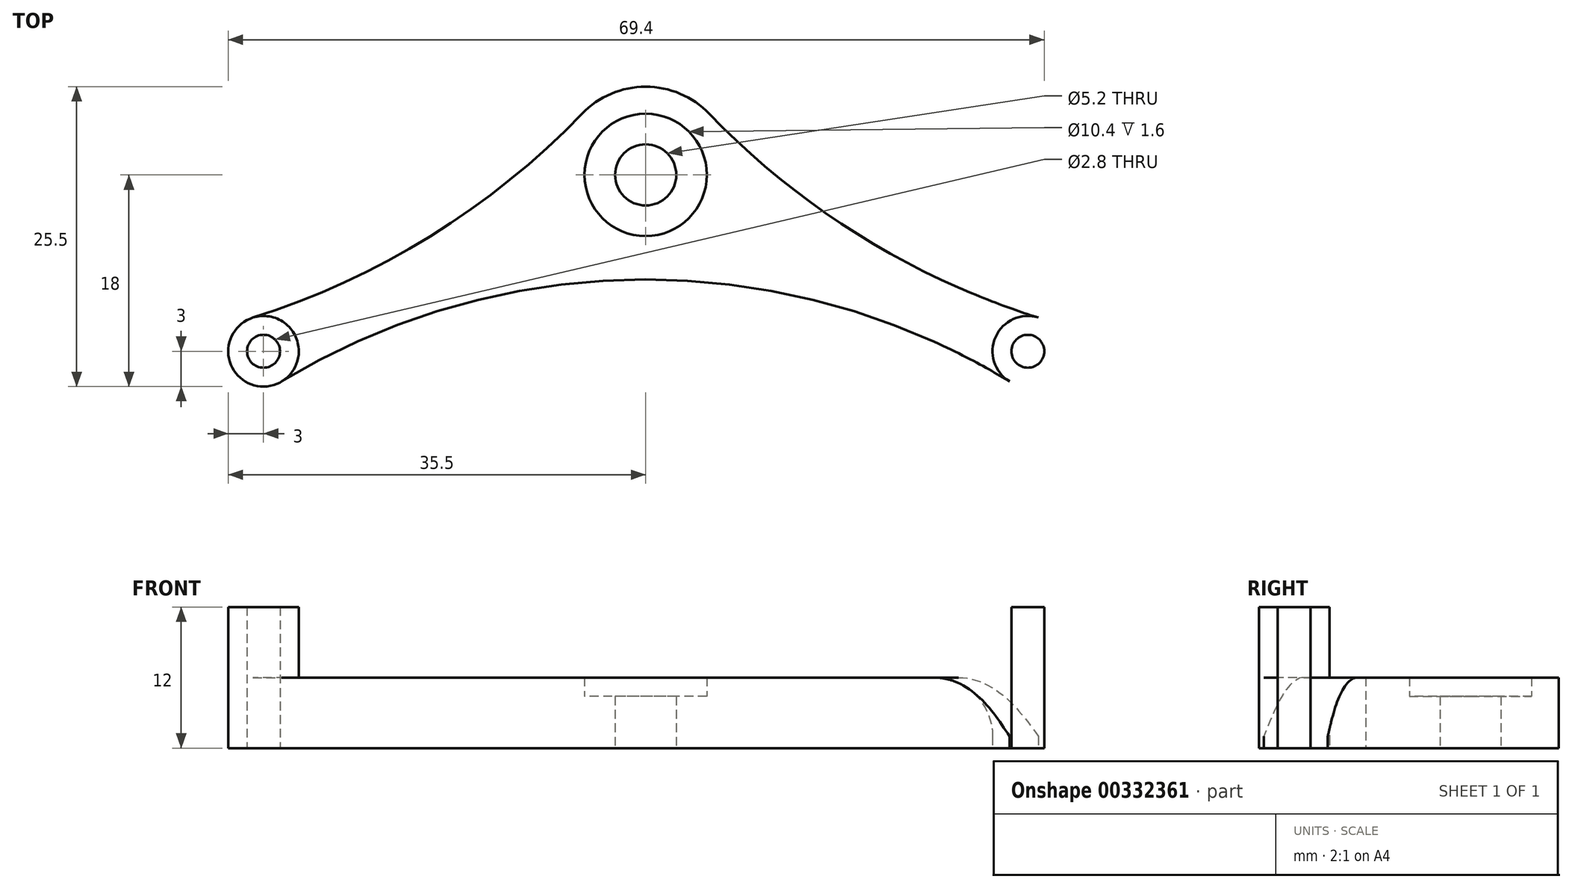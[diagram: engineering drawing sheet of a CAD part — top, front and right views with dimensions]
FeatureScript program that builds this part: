
annotation { "Feature Type Name" : "Feature", "Feature Type Description" : "" }
export const myFeature = defineFeature(function(context is Context, id is Id, definition is map)
    precondition{}
    {
        {
            var Q0;
            Q0=qCreatedBy(makeId("Top.planeOp"),FACE);
            var sketch = newSketch(context, id + "F0", { "sketchPlane" : qUnion([Q0])});
            skCircle(sketch, "E0", {"center": v(-32.5, 0) * mm, "radius": 1.4 * mm});
            skCircle(sketch, "E1.MirrorC", {"center": v(32.5, 0) * mm, "radius": 1.4 * mm});
            skCircle(sketch, "E2", {"center": v(-32.5, 0) * mm, "radius": 3 * mm});
            skCircle(sketch, "E3", {"center": v(0, 15) * mm, "radius": 2.6 * mm});
            skCircle(sketch, "E4", {"center": v(0, 15) * mm, "radius": 5.2 * mm});
            skCircle(sketch, "E5", {"center": v(0, 15) * mm, "radius": 7.5 * mm});
            skArc(sketch, "E6", {"start": v(-33.4, 2.86) * mm, "mid": v(-18.31, 9.78) * mm, "end": v(-5.4, 20.2) * mm});
            skArc(sketch, "E7.MirrorCS", {"start": v(33.4, 2.86) * mm, "mid": v(18.31, 9.78) * mm, "end": v(5.4, 20.2) * mm});
            skCircle(sketch, "E8.MirrorC", {"center": v(32.5, 0) * mm, "radius": 3 * mm});
            skArc(sketch, "E9", {"start": v(30.94, -2.56) * mm, "mid": v(0, 6.1) * mm, "end": v(-30.94, -2.56) * mm});
            skSolve(sketch);
        }
        {
            var Q0;
            Q0=makeQuery(id+"F0.imprint","IMPRINT",FACE,{"disambiguationData":[TD([[makeQuery(id+"F0.imprint","IMPRINT",EDGE,{"derivedFrom":sQuery(id+"F0.wireOp",EDGE,"E3")}),-1.0]])]});
            extrude(context, id + "F1", {"entities" : qUnion([Q0]), "depth" : 4.4 * mm, "offsetDistance" : 25 * mm});
        }
        {
            var Q0;
            {var subQ0=sQuery(id+"F0.wireOp",EDGE,"E6");Q0=makeQuery(id+"F0.imprint","IMPRINT",FACE,{"disambiguationData":[TD([[makeQuery(id+"F0.imprint","IMPRINT",EDGE,{"derivedFrom":subQ0}),-1.0]])]});}
            var Q1;
            Q1=makeQuery(id+"F0.imprint","IMPRINT",FACE,{"disambiguationData":[TD([[makeQuery(id+"F0.imprint","IMPRINT",EDGE,{"derivedFrom":sQuery(id+"F0.wireOp",EDGE,"E4")}),-1.0]])]});
            var Q2;
            {var subQ1=sQuery(id+"F0.wireOp",EDGE,"E7.MirrorCS");Q2=makeQuery(id+"F0.imprint","IMPRINT",FACE,{"disambiguationData":[TD([[makeQuery(id+"F0.imprint","IMPRINT",EDGE,{"derivedFrom":subQ1}),1.0]])]});}
            extrude(context, id + "F2", {"entities" : qUnion([Q0, Q1, Q2]), "operationType" : NewBodyOperationType.ADD, "depth" : 6 * mm, "offsetDistance" : 25 * mm});
        }
        {
            var Q0;
            Q0=makeQuery(id+"F0.imprint","IMPRINT",FACE,{"disambiguationData":[TD([[makeQuery(id+"F0.imprint","IMPRINT",EDGE,{"derivedFrom":sQuery(id+"F0.wireOp",EDGE,"E0")}),-1.0]])]});
            var Q1;
            Q1=makeQuery(id+"F0.imprint","IMPRINT",FACE,{"disambiguationData":[TD([[makeQuery(id+"F0.imprint","IMPRINT",EDGE,{"derivedFrom":sQuery(id+"F0.wireOp",EDGE,"E1.MirrorC")}),1.0]])]});
            extrude(context, id + "F3", {"entities" : qUnion([Q0, Q1]), "operationType" : NewBodyOperationType.ADD, "depth" : 12 * mm, "offsetDistance" : 25 * mm});
        }
        {
            var Q0;
            Q0=makeQuery(id+"F2.opExtrude","CAP_EDGE",EDGE,{"disambiguationData":[OSD([sQuery(id+"F0.wireOp",EDGE,"E2")])],"isStart":false});
            var Q1;
            Q1=makeQuery(id+"F2.opExtrude","CAP_EDGE",EDGE,{"disambiguationData":[OSD([sQuery(id+"F0.wireOp",EDGE,"E8.MirrorC")])],"isStart":false});
            fillet(context, id + "F4", {"entities" : qUnion([Q0, Q1]), "tangentPropagation" : true, "radius" : 5 * mm, "defaultsChanged" : false, "vertexSettings" : [], "allowEdgeOverflow" : false});
        }
    });
